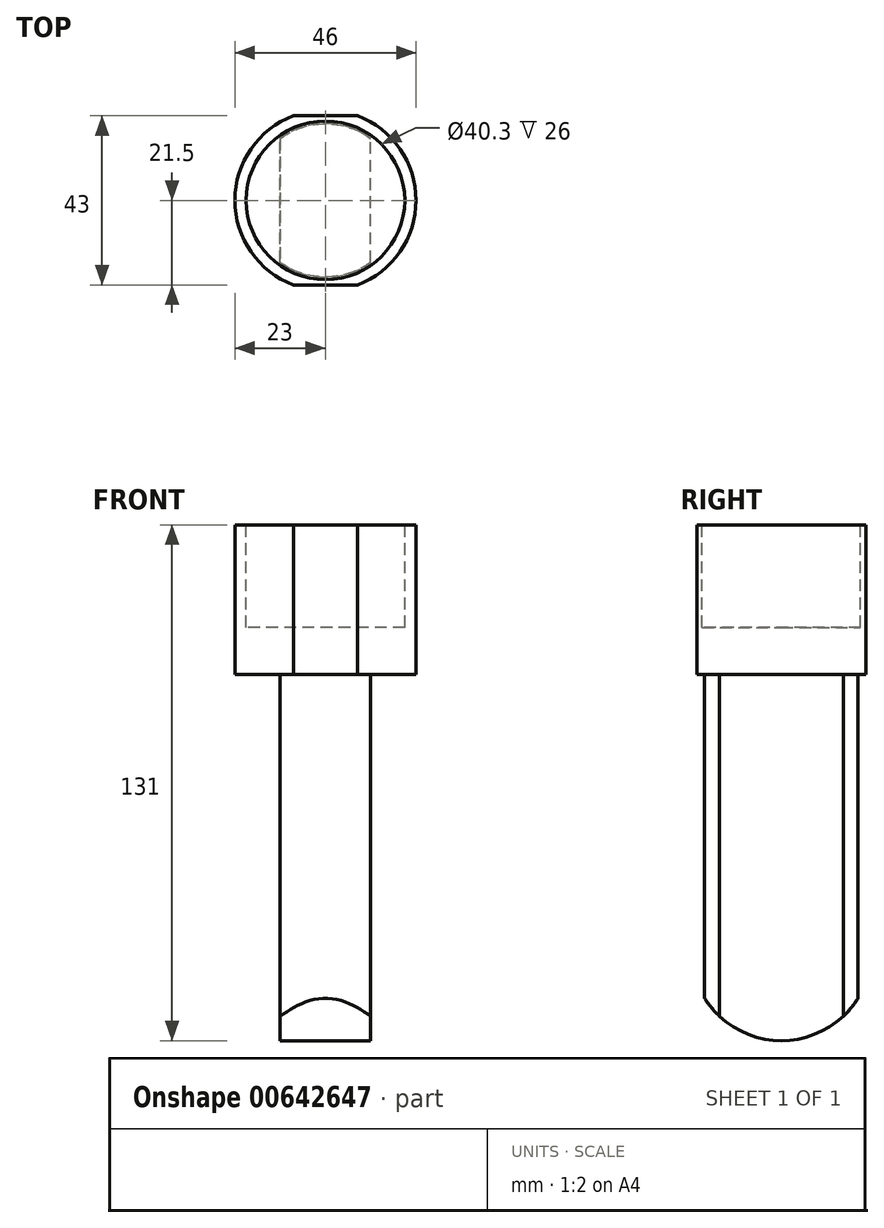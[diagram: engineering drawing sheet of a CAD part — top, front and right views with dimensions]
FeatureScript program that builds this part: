
annotation { "Feature Type Name" : "Feature", "Feature Type Description" : "" }
export const myFeature = defineFeature(function(context is Context, id is Id, definition is map)
    precondition{}
    {
        {
            var Q0;
            Q0=qCreatedBy(makeId("Top.planeOp"),FACE);
            var sketch = newSketch(context, id + "F0", { "sketchPlane" : qUnion([Q0])});
            skArc(sketch, "E0", {"start": v(-8.17, 21.5) * mm, "mid": v(-23, 0) * mm, "end": v(-8.17, -21.5) * mm});
            skLineSegment(sketch, "E1", {"start": v(-8.17, 21.5) * mm, "end": v(8.17, 21.5) * mm});
            skLineSegment(sketch, "E2.MirrorCS", {"start": v(-8.17, -21.5) * mm, "end": v(8.17, -21.5) * mm});
            skArc(sketch, "E3.trimOffspring", {"start": v(8.17, -21.5) * mm, "mid": v(23, 0) * mm, "end": v(8.17, 21.5) * mm});
            skSolve(sketch);
        }
        {
            var Q0;
            Q0=makeQuery(id+"F0.imprint","IMPRINT",FACE,{"disambiguationData":[TD([[makeQuery(id+"F0.imprint","IMPRINT",EDGE,{"derivedFrom":sQuery(id+"F0.wireOp",EDGE,"E0")}),1.0]])]});
            extrude(context, id + "F1", {"entities" : qUnion([Q0]), "depth" : 38 * mm, "offsetDistance" : 25 * mm});
        }
        {
            var Q0;
            Q0=makeQuery(id+"F1.opExtrude","CAP_FACE",FACE,{"disambiguationData":[OSD([sQuery(id+"F0.wireOp",EDGE,"E0"),sQuery(id+"F0.wireOp",EDGE,"E1"),sQuery(id+"F0.wireOp",EDGE,"E2.MirrorCS"),sQuery(id+"F0.wireOp",EDGE,"E3.trimOffspring")])],"isStart":false});
            var sketch = newSketch(context, id + "F2", { "sketchPlane" : qUnion([Q0])});
            skCircle(sketch, "E4", {"center": v(0, 0) * mm, "radius": 20.15 * mm});
            skSolve(sketch);
        }
        {
            var Q0;
            Q0=makeQuery(id+"F2.imprint","IMPRINT",FACE,{"disambiguationData":[TD([[makeQuery(id+"F2.imprint","IMPRINT",EDGE,{"derivedFrom":sQuery(id+"F2.wireOp",EDGE,"E4")}),1.0]])]});
            extrude(context, id + "F3", {"entities" : qUnion([Q0]), "operationType" : NewBodyOperationType.REMOVE, "oppositeDirection" : true, "depth" : 26 * mm, "offsetDistance" : 25 * mm});
        }
        {
            var Q0;
            Q0=makeQuery(id+"F1.opExtrude","CAP_FACE",FACE,{"disambiguationData":[OSD([sQuery(id+"F0.wireOp",EDGE,"E0"),sQuery(id+"F0.wireOp",EDGE,"E1"),sQuery(id+"F0.wireOp",EDGE,"E2.MirrorCS"),sQuery(id+"F0.wireOp",EDGE,"E3.trimOffspring")])],"isStart":true});
            var sketch = newSketch(context, id + "F4", { "sketchPlane" : qUnion([Q0])});
            skArc(sketch, "E5", {"start": v(-11.5, -15.75) * mm, "mid": v(0, -19.5) * mm, "end": v(11.5, -15.75) * mm});
            skLineSegment(sketch, "E6", {"start": v(-11.5, 15.75) * mm, "end": v(-11.5, -15.75) * mm});
            skLineSegment(sketch, "E7.MirrorCS", {"start": v(11.5, 15.75) * mm, "end": v(11.5, -15.75) * mm});
            skArc(sketch, "E8.trimOffspring", {"start": v(11.5, 15.75) * mm, "mid": v(0, 19.5) * mm, "end": v(-11.5, 15.75) * mm});
            skSolve(sketch);
        }
        {
            var Q0;
            Q0=makeQuery(id+"F4.imprint","IMPRINT",FACE,{"disambiguationData":[TD([[makeQuery(id+"F4.imprint","IMPRINT",EDGE,{"derivedFrom":sQuery(id+"F4.wireOp",EDGE,"E5")}),1.0]])]});
            extrude(context, id + "F5", {"entities" : qUnion([Q0]), "operationType" : NewBodyOperationType.ADD, "depth" : 93 * mm, "offsetDistance" : 25 * mm});
        }
        {
            var Q0;
            Q0=makeQuery(id+"F5.opExtrude","SWEPT_FACE",FACE,{"disambiguationData":[OSD([sQuery(id+"F4.wireOp",EDGE,"E6")])]});
            var sketch = newSketch(context, id + "F6", { "sketchPlane" : qUnion([Q0])});
            skArc(sketch, "E9", {"start": v(-19.67, -81.93) * mm, "mid": v(0, -93) * mm, "end": v(19.67, -81.93) * mm});
            skLineSegment(sketch, "E10", {"start": v(-19.67, -81.93) * mm, "end": v(19.67, -81.93) * mm});
            skLineSegment(sketch, "E11", {"start": v(-19.67, -81.93) * mm, "end": v(-31.85, -115.36) * mm});
            skLineSegment(sketch, "E12", {"start": v(-31.85, -115.36) * mm, "end": v(38.54, -119.63) * mm});
            skLineSegment(sketch, "E13", {"start": v(38.54, -119.63) * mm, "end": v(19.67, -81.93) * mm});
            skSolve(sketch);
        }
        {
            var Q0;
            {var subQ0=sQuery(id+"F6.wireOp",EDGE,"E11");Q0=makeQuery(id+"F6.imprint","IMPRINT",FACE,{"disambiguationData":[TD([[makeQuery(id+"F6.imprint","IMPRINT",EDGE,{"derivedFrom":subQ0}),1.0]])]});}
            var Q1;
            {var subQ0=sQuery(id+"F6.wireOp",EDGE,"E9");var subQ1=sQuery(id+"F4.wireOp",EDGE,"E6");var subQ4=makeQuery(id+"F5.opExtrude","CAP_EDGE",EDGE,{"disambiguationData":[OSD([subQ1])],"isStart":false});var subQ5=makeQuery(id+"F6.imprint","INTERSECT",VERTEX,{"derivedFrom":[subQ4,subQ0]});Q1=makeQuery(id+"F6.imprint","IMPRINT",FACE,{"disambiguationData":[TD([[makeQuery(id+"F6.imprint","IMPRINT",EDGE,{"disambiguationData":[TD([[subQ5,1.0]])],"derivedFrom":subQ0}),-1.0]])]});}
            var Q2;
            {var subQ0=sQuery(id+"F6.wireOp",EDGE,"E9");var subQ1=sQuery(id+"F4.wireOp",EDGE,"E6");var subQ2=makeQuery(id+"F5.opExtrude","CAP_EDGE",EDGE,{"disambiguationData":[OSD([subQ1])],"isStart":false});var subQ3=makeQuery(id+"F6.imprint","INTERSECT",VERTEX,{"derivedFrom":[subQ2,subQ0]});Q2=makeQuery(id+"F6.imprint","IMPRINT",FACE,{"disambiguationData":[TD([[makeQuery(id+"F6.imprint","IMPRINT",EDGE,{"disambiguationData":[TD([[subQ3,-1.0]])],"derivedFrom":subQ0}),-1.0]])]});}
            extrude(context, id + "F7", {"entities" : qUnion([Q0, Q1, Q2]), "operationType" : NewBodyOperationType.REMOVE, "endBound" : BoundingType.THROUGH_ALL, "oppositeDirection" : true, "depth" : 25 * mm, "offsetDistance" : 25 * mm});
        }
    });
